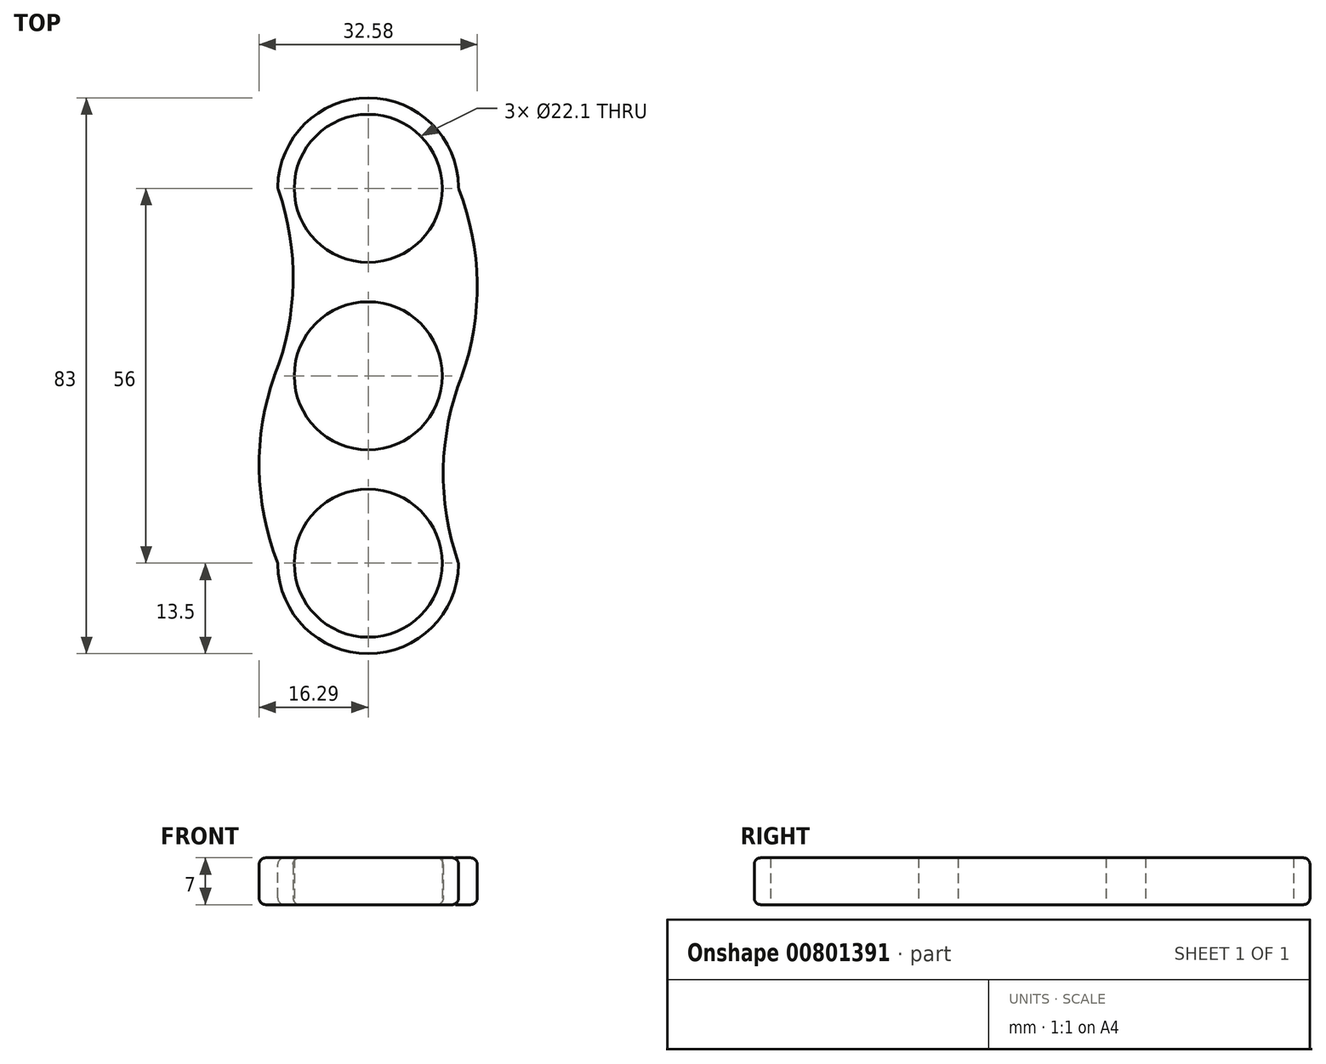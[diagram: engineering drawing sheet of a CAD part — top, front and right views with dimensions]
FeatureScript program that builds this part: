
annotation { "Feature Type Name" : "Feature", "Feature Type Description" : "" }
export const myFeature = defineFeature(function(context is Context, id is Id, definition is map)
    precondition{}
    {
        {
            var Q0;
            Q0=qCreatedBy(makeId("Top.planeOp"),FACE);
            var sketch = newSketch(context, id + "F0", { "sketchPlane" : qUnion([Q0])});
            skCircle(sketch, "E0", {"center": v(0, 0) * mm, "radius": 11.05 * mm});
            skCircle(sketch, "E1", {"center": v(0, 0) * mm, "radius": 14 * mm});
            skLineSegment(sketch, "E2", {"start": v(0, 14) * mm, "end": v(0, 28) * mm, "construction": true});
            skCircle(sketch, "E3", {"center": v(0, 28) * mm, "radius": 11.05 * mm});
            skCircle(sketch, "E4", {"center": v(0, 28) * mm, "radius": 13.5 * mm});
            skLineSegment(sketch, "E5", {"start": v(14, 0) * mm, "end": v(-14, 0) * mm, "construction": true});
            skLineSegment(sketch, "E6", {"start": v(-13.5, 28) * mm, "end": v(13.5, 28) * mm, "construction": true});
            skArc(sketch, "E7", {"start": v(-14, 0) * mm, "mid": v(-11.22, 13.95) * mm, "end": v(-13.5, 28) * mm});
            skArc(sketch, "E8", {"start": v(14, 0) * mm, "mid": v(16.28, 14.05) * mm, "end": v(13.5, 28) * mm});
            skCircle(sketch, "E9.1.0", {"center": v(0, -28) * mm, "radius": 13.5 * mm});
            skCircle(sketch, "E9.1.1", {"center": v(0, -28) * mm, "radius": 11.05 * mm});
            skArc(sketch, "E9.1.2", {"start": v(14, 0) * mm, "mid": v(11.22, -13.95) * mm, "end": v(13.5, -28) * mm});
            skArc(sketch, "E9.1.3", {"start": v(-14, 0) * mm, "mid": v(-16.28, -14.05) * mm, "end": v(-13.5, -28) * mm});
            skSolve(sketch);
        }
        {
            var Q0;
            Q0=makeQuery(id+"F0.imprint","IMPRINT",FACE,{"disambiguationData":[TD([[makeQuery(id+"F0.imprint","IMPRINT",EDGE,{"derivedFrom":sQuery(id+"F0.wireOp",EDGE,"E3")}),-1.0]])]});
            var Q1;
            {var subQ0=sQuery(id+"F0.wireOp",EDGE,"E8");Q1=makeQuery(id+"F0.imprint","IMPRINT",FACE,{"disambiguationData":[TD([[makeQuery(id+"F0.imprint","IMPRINT",EDGE,{"derivedFrom":subQ0}),1.0]])]});}
            var Q2;
            Q2=makeQuery(id+"F0.imprint","IMPRINT",FACE,{"disambiguationData":[TD([[makeQuery(id+"F0.imprint","IMPRINT",EDGE,{"derivedFrom":sQuery(id+"F0.wireOp",EDGE,"E0")}),-1.0]])]});
            var Q3;
            {var subQ0=sQuery(id+"F0.wireOp",EDGE,"E9.1.3");Q3=makeQuery(id+"F0.imprint","IMPRINT",FACE,{"disambiguationData":[TD([[makeQuery(id+"F0.imprint","IMPRINT",EDGE,{"derivedFrom":subQ0}),1.0]])]});}
            var Q4;
            Q4=makeQuery(id+"F0.imprint","IMPRINT",FACE,{"disambiguationData":[TD([[makeQuery(id+"F0.imprint","IMPRINT",EDGE,{"derivedFrom":sQuery(id+"F0.wireOp",EDGE,"E9.1.1")}),-1.0]])]});
            extrude(context, id + "F1", {"entities" : qUnion([Q0, Q1, Q2, Q3, Q4]), "depth" : 7 * mm, "offsetDistance" : 25 * mm});
        }
        {
            var Q0;
            Q0=makeQuery(id+"F1.opExtrude","SWEPT_FACE",FACE,{"disambiguationData":[OSD([sQuery(id+"F0.wireOp",EDGE,"E8")])]});
            var Q1;
            Q1=makeQuery(id+"F1.opExtrude","SWEPT_FACE",FACE,{"disambiguationData":[OSD([sQuery(id+"F0.wireOp",EDGE,"E4")])]});
            var Q2;
            Q2=makeQuery(id+"F1.opExtrude","SWEPT_FACE",FACE,{"disambiguationData":[OSD([sQuery(id+"F0.wireOp",EDGE,"E7")])]});
            var Q3;
            Q3=makeQuery(id+"F1.opExtrude","SWEPT_FACE",FACE,{"disambiguationData":[OSD([sQuery(id+"F0.wireOp",EDGE,"E9.1.3")])]});
            var Q4;
            Q4=makeQuery(id+"F1.opExtrude","SWEPT_FACE",FACE,{"disambiguationData":[OSD([sQuery(id+"F0.wireOp",EDGE,"E9.1.0")])]});
            var Q5;
            Q5=makeQuery(id+"F1.opExtrude","SWEPT_FACE",FACE,{"disambiguationData":[OSD([sQuery(id+"F0.wireOp",EDGE,"E9.1.2")])]});
            fillet(context, id + "F2", {"entities" : qUnion([Q0, Q1, Q2, Q3, Q4, Q5]), "radius" : 1 * mm, "tangentPropagation" : true, "allowEdgeOverflow" : false});
        }
    });
